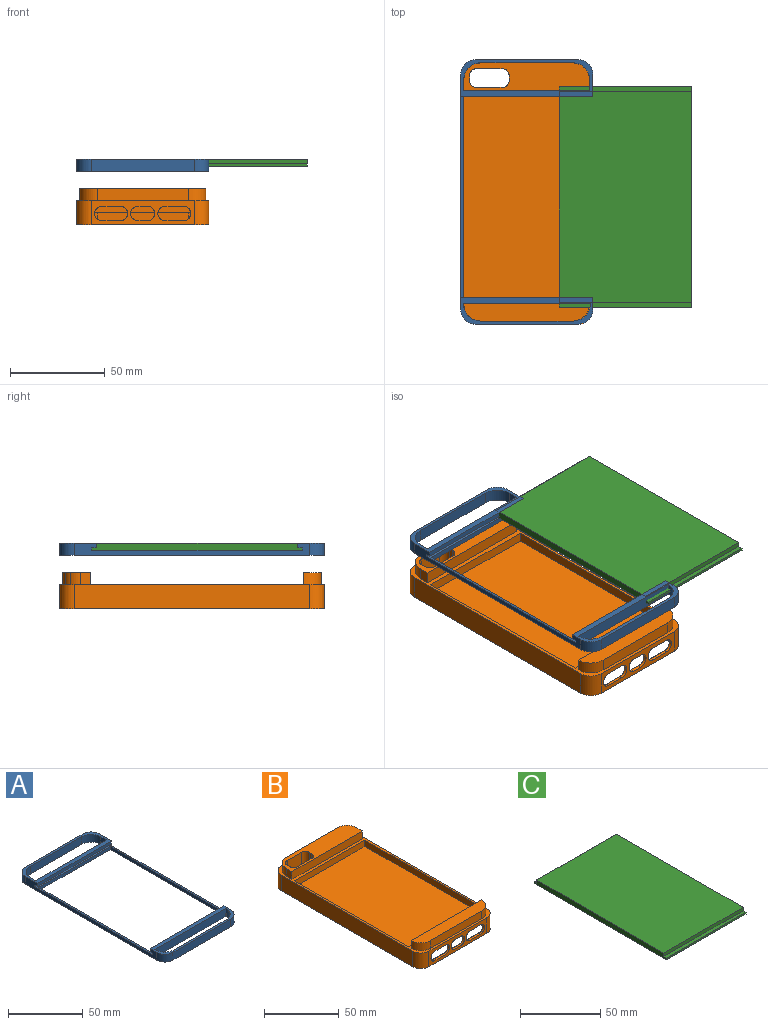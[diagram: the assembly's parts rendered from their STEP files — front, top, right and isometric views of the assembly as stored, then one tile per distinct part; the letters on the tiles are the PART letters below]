
ASSEMBLY  parts=3 mates=2
PART A: 34 faces, bbox 69.9x139.7x6.4 mm
  f0: plane 69.85x19.26mm, normal (0,0,1), area 387.8mm2, adj f1,f2,f3,f7,f9,f12,f13,f14
  f1: plane 124.46x6.35mm, normal (-1,0,0), area 378.2mm2, adj f0,f3,f4,f5,f6,f9,f10,f29
  f2: plane 124.46x6.35mm, normal (1,0,0), area 378.2mm2, adj f0,f3,f4,f5,f6,f11,f12,f29
  f3: plane 69.85x2.54mm, normal (0,-1,0), area 177.4mm2, adj f0,f1,f2,f33
  f4: plane 69.85x2.54mm, normal (0,1,0), area 177.4mm2, adj f1,f2,f5,f29
  f5: plane 69.85x13.97mm, normal (0,0,1), area 367mm2, adj f1,f2,f4,f8,f10,f11,f19,f20
  f6: plane 139.7x69.85mm, normal (0,0,-1), area 1025.3mm2, adj f1,f2,f7,f8,f9,f10,f11,f12
  f7: plane 54.61x6.35mm, normal (0,1,0), area 346.8mm2, adj f0,f6,f9,f12
  f8: plane 54.61x6.35mm, normal (0,-1,0), area 346.8mm2, adj f5,f6,f10,f11
  f9: cylinder r=7.62mm len=7.62mm, axis (0,0,1), area 76mm2, adj f0,f1,f6,f7
  f10: cylinder r=7.62mm len=7.62mm, axis (0,0,-1), area 76mm2, adj f1,f5,f6,f8
  f11: cylinder r=7.62mm len=7.62mm, axis (0,0,1), area 76mm2, adj f2,f5,f6,f8
  f12: cylinder r=7.62mm len=7.62mm, axis (0,0,-1), area 76mm2, adj f0,f2,f6,f7
  f13: plane 6.35x5.35mm, normal (1,0,0), area 34mm2, adj f0,f6,f14,f18
  f14: plane 66.8x6.35mm, normal (0,1,0), area 424.2mm2, adj f0,f6,f13,f15
  f15: plane 6.35x5.35mm, normal (-1,0,0), area 34mm2, adj f0,f6,f14,f16
  f16: cylinder r=9.14mm len=9.14mm, axis (0,0,1), area 91.2mm2, adj f0,f6,f15,f17
  f17: plane 48.51x6.35mm, normal (0,-1,0), area 308.1mm2, adj f0,f6,f16,f18
  f18: cylinder r=9.14mm len=9.14mm, axis (0,0,1), area 91.2mm2, adj f0,f6,f13,f17
  f19: cylinder r=9.14mm len=9.14mm, axis (0,0,1), area 91.2mm2, adj f5,f6,f20,f24
  f20: plane 49.02x6.35mm, normal (0,1,0), area 311.3mm2, adj f5,f6,f19,f21
  f21: cylinder r=9.14mm len=9.14mm, axis (0,0,1), area 91.2mm2, adj f5,f6,f20,f22
  f22: plane 6.35x0.06mm, normal (-1,0,0), area 0.4mm2, adj f5,f6,f21,f23
  f23: plane 67.31x6.35mm, normal (0,-1,0), area 427.4mm2, adj f5,f6,f22,f24
  f24: plane 6.35x0.06mm, normal (1,0,0), area 0.4mm2, adj f5,f6,f19,f23
  f25: plane 67.31x2.54mm, normal (0,-1,0), area 171mm2, adj f6,f26,f28,f31
  f26: plane 106.47x2.54mm, normal (1,0,0), area 270.4mm2, adj f6,f25,f27,f31
  f27: plane 67.31x2.54mm, normal (0,1,0), area 171mm2, adj f6,f26,f28,f31
  f28: plane 106.47x2.54mm, normal (-1,0,0), area 270.4mm2, adj f6,f25,f27,f31
  f29: plane 69.85x2.54mm, normal (0,0,-1), area 177.4mm2, adj f1,f2,f4,f30
  f30: plane 69.85x1.27mm, normal (0,1,0), area 88.7mm2, adj f1,f2,f29,f31
  f31: plane 111.55x69.85mm, normal (0,0,1), area 625.3mm2, adj f1,f2,f25,f26,f27,f28,f30,f32
  f32: plane 69.85x1.27mm, normal (0,-1,0), area 88.7mm2, adj f1,f2,f31,f33
  f33: plane 69.85x2.54mm, normal (0,0,-1), area 177.4mm2, adj f1,f2,f3,f32
PART B: 90 faces, bbox 69.9x139.7x19.1 mm
  f0: plane 139.7x69.85mm, normal (0,0,1), area 1002.9mm2, adj f4,f6,f10,f11,f12,f13,f14,f15
  f1: plane 66.68x14.49mm, normal (0,0,1), area 734.5mm2, adj f6,f39,f40,f41,f42,f43,f44,f49
  f2: plane 136.53x66.68mm, normal (0,0,1), area 612.1mm2, adj f7,f8,f17,f18,f19,f20,f21,f22
  f3: plane 125.73x66.68mm, normal (0,0,-1), area 7634.3mm2, adj f23,f27,f30,f37,f45,f46,f47,f48
  f4: plane 124.46x12.7mm, normal (-1,0,0), area 1580.6mm2, adj f0,f9,f13,f14
  f5: plane 10.45x1.59mm, normal (0,0,-1), area 12.2mm2, adj f27,f45,f48,f60
  f6: cylinder r=9.21mm len=6.35mm, axis (0,0,-1), area 34.8mm2, adj f0,f1,f40,f49
  f7: cylinder r=7.62mm len=7.62mm, axis (0,0,-1), area 9.5mm2, adj f2,f8,f9,f17
  f8: plane 118.11x0.79mm, normal (-1,0,0), area 93.7mm2, adj f2,f7,f9,f22
  f9: plane 139.7x69.85mm, normal (0,0,-1), area 1290.3mm2, adj f4,f7,f8,f10,f11,f12,f13,f14
  f10: plane 54.61x12.7mm, normal (0,1,0), area 693.5mm2, adj f0,f9,f13,f16
  f11: plane 54.61x12.7mm, normal (0,-1,0), area 366.8mm2, adj f0,f9,f14,f15,f61,f62,f63,f64
  f12: plane 124.46x12.7mm, normal (1,0,0), area 1580.6mm2, adj f0,f9,f15,f16
  f13: cylinder r=7.62mm len=12.7mm, axis (0,0,1), area 152mm2, adj f0,f4,f9,f10
  f14: cylinder r=7.62mm len=12.7mm, axis (0,0,-1), area 152mm2, adj f0,f4,f9,f11
  f15: cylinder r=7.62mm len=12.7mm, axis (0,0,1), area 152mm2, adj f0,f9,f11,f12
  f16: cylinder r=7.62mm len=12.7mm, axis (0,0,-1), area 152mm2, adj f0,f9,f10,f12
  f17: plane 48.26x0.79mm, normal (0,1,0), area 38.3mm2, adj f2,f7,f9,f20
  f18: plane 118.11x0.79mm, normal (1,0,0), area 93.7mm2, adj f2,f9,f20,f21
  f19: plane 48.26x0.79mm, normal (0,-1,0), area 38.3mm2, adj f2,f9,f21,f22
  f20: cylinder r=7.62mm len=7.62mm, axis (0,0,-1), area 9.5mm2, adj f2,f9,f17,f18
  f21: cylinder r=7.62mm len=7.62mm, axis (0,0,1), area 9.5mm2, adj f2,f9,f18,f19
  f22: cylinder r=7.62mm len=7.62mm, axis (0,0,1), area 9.5mm2, adj f2,f8,f9,f19
  f23: plane 118.11x9.37mm, normal (-1,0,0), area 676.4mm2, adj f2,f3,f24,f29,f37,f38
  f24: cylinder r=9.21mm len=9.37mm, axis (0,0,-1), area 130.3mm2, adj f2,f23,f25,f30,f31,f77,f78,f82
  f25: plane 48.26x9.37mm, normal (0,1,0), area 135.6mm2, adj f2,f24,f26,f31,f61,f62,f63,f65
  f26: cylinder r=9.21mm len=9.37mm, axis (0,0,-1), area 130.3mm2, adj f2,f25,f30,f31,f60,f64,f65,f66
  f27: cylinder r=9.21mm len=9.37mm, axis (0,0,-1), area 122.2mm2, adj f2,f3,f5,f28,f38,f45,f46,f60
  f28: plane 48.26x9.37mm, normal (0,-1,0), area 452mm2, adj f2,f27,f29,f38
  f29: cylinder r=9.21mm len=9.37mm, axis (0,0,1), area 135.5mm2, adj f2,f23,f28,f38
  f30: plane 66.68x3.81mm, normal (0,-1,0), area 254mm2, adj f3,f24,f26,f31
  f31: plane 66.68x9.21mm, normal (0,0,-1), area 577.5mm2, adj f24,f25,f26,f30
  f32: cylinder r=9.21mm len=9.21mm, axis (0,0,-1), area 91.8mm2, adj f0,f33,f35,f36
  f33: plane 66.68x6.35mm, normal (0,1,0), area 423.4mm2, adj f0,f32,f34,f36
  f34: cylinder r=9.21mm len=9.21mm, axis (0,0,-1), area 91.8mm2, adj f0,f33,f35,f36
  f35: plane 48.26x6.35mm, normal (0,-1,0), area 306.5mm2, adj f0,f32,f34,f36
  f36: plane 66.68x9.21mm, normal (0,0,1), area 577.5mm2, adj f32,f33,f34,f35
  f37: plane 36.12x3.81mm, normal (0,1,0), area 137.6mm2, adj f3,f23,f38,f51
  f38: plane 62.64x14.49mm, normal (0,0,-1), area 610.3mm2, adj f23,f27,f28,f29,f37,f46,f47,f50
  f39: plane 66.68x6.35mm, normal (0,-1,0), area 423.4mm2, adj f0,f1,f40,f44
  f40: plane 6.35x5.29mm, normal (-1,0,0), area 33.6mm2, adj f0,f1,f6,f39
  f41: cylinder r=9.21mm len=6.35mm, axis (0,0,-1), area 34.8mm2, adj f0,f1,f42,f49
  f42: plane 48.26x6.35mm, normal (0,1,0), area 306.5mm2, adj f0,f1,f41,f43
  f43: cylinder r=9.21mm len=9.21mm, axis (0,0,-1), area 91.8mm2, adj f0,f1,f42,f44
  f44: plane 6.35x5.29mm, normal (1,0,0), area 33.6mm2, adj f0,f1,f39,f43
  f45: plane 6.77x3.81mm, normal (-1,0,0), area 25.8mm2, adj f3,f5,f27,f48
  f46: plane 16.36x3.81mm, normal (0,1,0), area 62.3mm2, adj f3,f27,f38,f50
  f47: plane 3.81x2.75mm, normal (1,0,0), area 10.5mm2, adj f3,f38,f50,f51
  f48: cylinder r=5.08mm len=3.81mm, axis (0,0,1), area 15.7mm2, adj f3,f5,f45,f60
  f49: cylinder r=5.08mm len=6.35mm, axis (0,0,-1), area 22.5mm2, adj f0,f1,f6,f41
  f50: cylinder r=5.08mm len=5.08mm, axis (0,0,1), area 30.4mm2, adj f3,f38,f46,f47
  f51: cylinder r=5.08mm len=5.08mm, axis (0,0,-1), area 30.4mm2, adj f3,f37,f38,f47
  f52: plane 12.7x2.49mm, normal (1,0,0), area 31.6mm2, adj f1,f3,f53,f59
  f53: cylinder r=3.72mm len=12.7mm, axis (0,0,-1), area 74.2mm2, adj f1,f3,f52,f54
  f54: plane 13.47x12.7mm, normal (0,-1,0), area 171.1mm2, adj f1,f3,f53,f55
  f55: cylinder r=3.72mm len=12.7mm, axis (0,0,-1), area 74.2mm2, adj f1,f3,f54,f56
  f56: plane 12.7x2.49mm, normal (-1,0,0), area 31.6mm2, adj f1,f3,f55,f57
  f57: cylinder r=3.72mm len=12.7mm, axis (0,0,-1), area 74.2mm2, adj f1,f3,f56,f58
  f58: plane 13.47x12.7mm, normal (0,1,0), area 171.1mm2, adj f1,f3,f57,f59
  f59: cylinder r=3.72mm len=12.7mm, axis (0,0,-1), area 74.2mm2, adj f1,f3,f52,f58
  f60: plane 118.11x9.37mm, normal (1,0,0), area 676.4mm2, adj f2,f3,f5,f26,f27,f48
  f61: plane 9.99x1.59mm, normal (0,0,1), area 15.9mm2, adj f11,f25,f62,f65
  f62: cylinder r=3.72mm len=3.72mm, axis (0,-1,0), area 9.3mm2, adj f11,f25,f61,f63
  f63: plane 1.59x0.18mm, normal (-1,0,0), area 0.3mm2, adj f11,f25,f62,f68
  f64: plane 1.68x0.18mm, normal (1,0,0), area 0.3mm2, adj f11,f26,f65,f66
  f65: cylinder r=3.72mm len=3.72mm, axis (0,-1,0), area 9.4mm2, adj f11,f25,f26,f61,f64
  f66: cylinder r=3.72mm len=3.72mm, axis (0,-1,0), area 9.4mm2, adj f11,f25,f26,f64,f67
  f67: plane 9.99x1.59mm, normal (0,0,-1), area 15.9mm2, adj f11,f25,f66,f68
  f68: cylinder r=3.72mm len=3.72mm, axis (0,-1,0), area 9.3mm2, adj f11,f25,f63,f67
  f69: cylinder r=3.72mm len=3.72mm, axis (0,-1,0), area 9.3mm2, adj f11,f25,f70,f73
  f70: plane 5.25x1.59mm, normal (0,0,1), area 8.3mm2, adj f11,f25,f69,f71
  f71: cylinder r=3.72mm len=3.72mm, axis (0,-1,0), area 9.3mm2, adj f11,f25,f70,f72
  f72: plane 1.59x0.18mm, normal (-1,0,0), area 0.3mm2, adj f11,f25,f71,f74
  f73: plane 1.59x0.18mm, normal (1,0,0), area 0.3mm2, adj f11,f25,f69,f76
  f74: cylinder r=3.72mm len=3.72mm, axis (0,-1,0), area 9.3mm2, adj f11,f25,f72,f75
  f75: plane 5.25x1.59mm, normal (0,0,-1), area 8.3mm2, adj f11,f25,f74,f76
  f76: cylinder r=3.72mm len=3.72mm, axis (0,-1,0), area 9.3mm2, adj f11,f25,f73,f75
  f77: plane 1.68x0.18mm, normal (-1,0,0), area 0.3mm2, adj f11,f24,f78,f82
  f78: cylinder r=3.72mm len=3.72mm, axis (0,-1,0), area 9.4mm2, adj f11,f24,f25,f77,f81
  f79: plane 1.59x0.18mm, normal (1,0,0), area 0.3mm2, adj f11,f25,f80,f84
  f80: cylinder r=3.72mm len=3.72mm, axis (0,-1,0), area 9.3mm2, adj f11,f25,f79,f81
  f81: plane 9.99x1.59mm, normal (0,0,1), area 15.9mm2, adj f11,f25,f78,f80
  f82: cylinder r=3.72mm len=3.72mm, axis (0,-1,0), area 9.4mm2, adj f11,f24,f25,f77,f83
  f83: plane 9.99x1.59mm, normal (0,0,-1), area 15.9mm2, adj f11,f25,f82,f84
  f84: cylinder r=3.72mm len=3.72mm, axis (0,-1,0), area 9.3mm2, adj f11,f25,f79,f83
  f85: plane 66.68x5.08mm, normal (0,-1,0), area 338.7mm2, adj f0,f86,f88,f89
  f86: plane 107.95x5.08mm, normal (1,0,0), area 548.4mm2, adj f0,f85,f87,f89
  f87: plane 66.68x5.08mm, normal (0,1,0), area 338.7mm2, adj f0,f86,f88,f89
  f88: plane 107.95x5.08mm, normal (-1,0,0), area 548.4mm2, adj f0,f85,f87,f89
  f89: plane 107.95x66.68mm, normal (0,0,1), area 7197.6mm2, adj f85,f86,f87,f88
PART C: 10 faces, bbox 69.9x116.6x3.8 mm
  f0: plane 111.55x69.85mm, normal (0,0,1), area 7792.1mm2, adj f1,f7,f8,f9
  f1: plane 69.85x2.54mm, normal (0,-1,0), area 177.4mm2, adj f0,f2,f8,f9
  f2: plane 69.85x2.54mm, normal (0,0,1), area 177.4mm2, adj f1,f3,f8,f9
  f3: plane 69.85x1.27mm, normal (0,-1,0), area 88.7mm2, adj f2,f4,f8,f9
  f4: plane 116.63x69.85mm, normal (0,0,-1), area 8146.9mm2, adj f3,f5,f8,f9
  f5: plane 69.85x1.27mm, normal (0,1,0), area 88.7mm2, adj f4,f6,f8,f9
  f6: plane 69.85x2.54mm, normal (0,0,1), area 177.4mm2, adj f5,f7,f8,f9
  f7: plane 69.85x2.54mm, normal (0,1,0), area 177.4mm2, adj f0,f6,f8,f9
  f8: plane 116.63x3.81mm, normal (1,0,0), area 431.5mm2, adj f0,f1,f2,f3,f4,f5,f6,f7
  f9: plane 116.63x3.81mm, normal (-1,0,0), area 431.5mm2, adj f0,f1,f2,f3,f4,f5,f6,f7
PLACE A t=(-92.37,-57.47,22.2)mm
PLACE B t=(-92.37,-57.47,-6.21)mm fixed
PLACE C t=(-75.23,-129.96,28.55)mm
MATE slider A.f6 <-> B.f0  axis (0,0,-1) through (-92.37,-73.55,22.2)mm
MATE slider C.f9 <-> A.f26  axis (-1,0,0) through (-75.23,-129.96,24.74)mm
